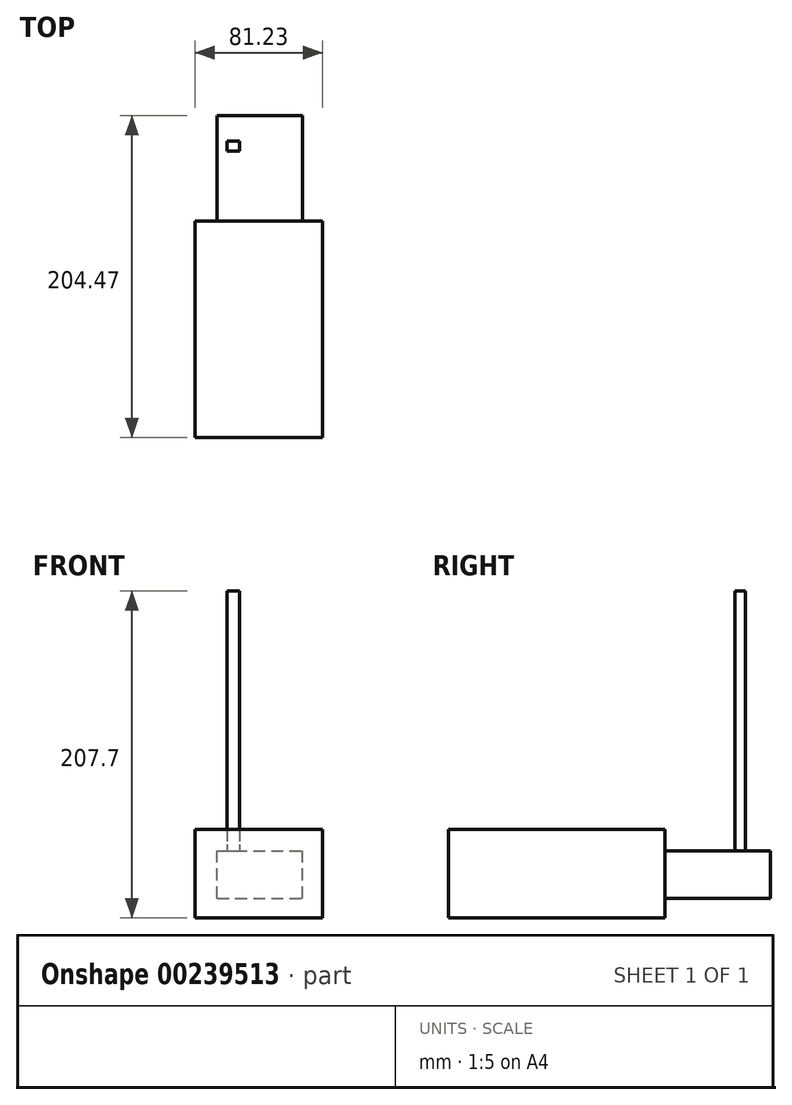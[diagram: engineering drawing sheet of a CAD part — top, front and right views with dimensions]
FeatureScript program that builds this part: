
annotation { "Feature Type Name" : "Feature", "Feature Type Description" : "" }
export const myFeature = defineFeature(function(context is Context, id is Id, definition is map)
    precondition{}
    {
        {
            var Q0;
            Q0=qCreatedBy(makeId("Front.planeOp"),FACE);
            var sketch = newSketch(context, id + "F0", { "sketchPlane" : qUnion([Q0])});
            skLineSegment(sketch, "E0.bottom", {"start": v(-33.3, 34.34) * mm, "end": v(47.94, 34.34) * mm});
            skLineSegment(sketch, "E0.top", {"start": v(-33.3, -21.79) * mm, "end": v(47.94, -21.79) * mm});
            skLineSegment(sketch, "E0.left", {"start": v(-33.3, 34.34) * mm, "end": v(-33.3, -21.79) * mm});
            skLineSegment(sketch, "E0.right", {"start": v(47.94, 34.34) * mm, "end": v(47.94, -21.79) * mm});
            skSolve(sketch);
        }
        {
            var Q0;
            Q0 = qSketchRegion(id + "F0", true);
            extrude(context, id + "F1", {"entities" : qUnion([Q0]), "endBound" : BoundingType.SYMMETRIC, "depth" : 137.4 * mm});
        }
        {
            var Q0;
            Q0=makeQuery(id+"F1.opExtrude","CAP_FACE",FACE,{"disambiguationData":[OSD([sQuery(id+"F0.wireOp",EDGE,"E0.bottom"),sQuery(id+"F0.wireOp",EDGE,"E0.top"),sQuery(id+"F0.wireOp",EDGE,"E0.left"),sQuery(id+"F0.wireOp",EDGE,"E0.right")])],"isStart":true});
            var sketch = newSketch(context, id + "F2", { "sketchPlane" : qUnion([Q0])});
            skLineSegment(sketch, "E1.bottom", {"start": v(19.12, -9.37) * mm, "end": v(-35.19, -9.37) * mm});
            skLineSegment(sketch, "E1.top", {"start": v(19.12, 20.8) * mm, "end": v(-35.19, 20.8) * mm});
            skLineSegment(sketch, "E1.left", {"start": v(19.12, -9.37) * mm, "end": v(19.12, 20.8) * mm});
            skLineSegment(sketch, "E1.right", {"start": v(-35.19, -9.37) * mm, "end": v(-35.19, 20.8) * mm});
            skSolve(sketch);
        }
        {
            var Q0;
            Q0 = qSketchRegion(id + "F2", true);
            extrude(context, id + "F3", {"entities" : qUnion([Q0]), "operationType" : NewBodyOperationType.ADD, "endBound" : BoundingType.SYMMETRIC, "depth" : 134.11 * mm});
        }
        {
            var Q0;
            Q0=makeQuery(id+"F3.opExtrude","SWEPT_FACE",FACE,{"disambiguationData":[OSD([sQuery(id+"F2.wireOp",EDGE,"E1.top")])]});
            var sketch = newSketch(context, id + "F4", { "sketchPlane" : qUnion([Q0])});
            skLineSegment(sketch, "E2.bottom", {"start": v(-12.87, 119.66) * mm, "end": v(-4.9, 119.66) * mm});
            skLineSegment(sketch, "E2.top", {"start": v(-12.87, 113.11) * mm, "end": v(-4.9, 113.11) * mm});
            skLineSegment(sketch, "E2.left", {"start": v(-12.87, 119.66) * mm, "end": v(-12.87, 113.11) * mm});
            skLineSegment(sketch, "E2.right", {"start": v(-4.9, 119.66) * mm, "end": v(-4.9, 113.11) * mm});
            skSolve(sketch);
        }
        {
            var Q0;
            Q0 = qSketchRegion(id + "F4", true);
            extrude(context, id + "F5", {"entities" : qUnion([Q0]), "operationType" : NewBodyOperationType.ADD, "depth" : 165.1 * mm});
        }
    });
